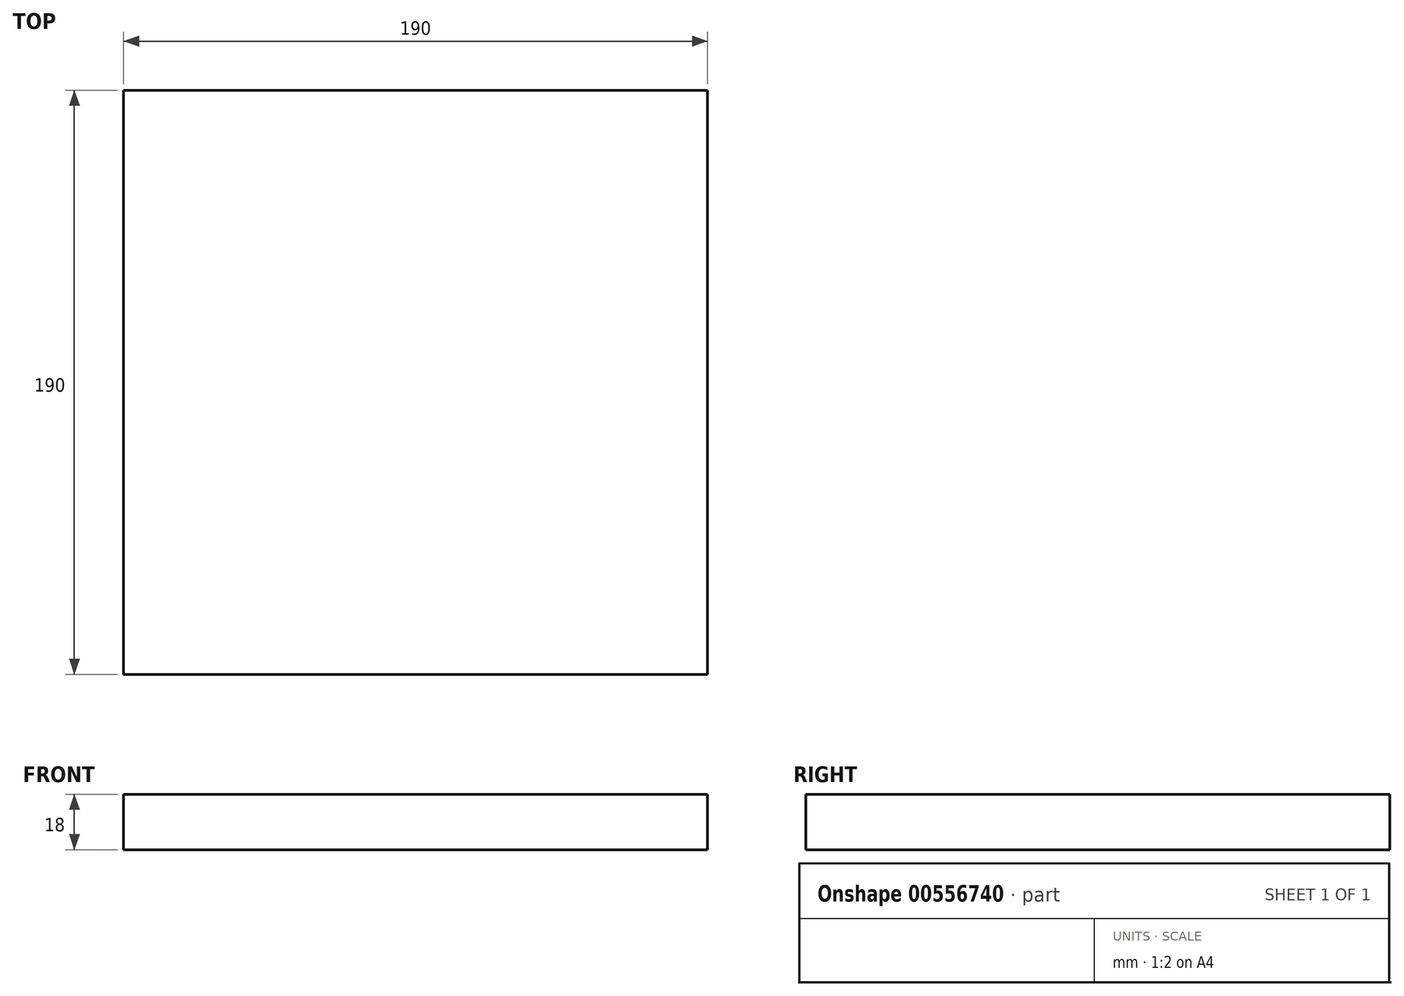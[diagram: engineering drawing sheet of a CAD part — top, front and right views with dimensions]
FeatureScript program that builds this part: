
annotation { "Feature Type Name" : "Feature", "Feature Type Description" : "" }
export const myFeature = defineFeature(function(context is Context, id is Id, definition is map)
    precondition{}
    {
        {
            var Q0;
            Q0=qCreatedBy(makeId("Top.planeOp"),FACE);
            var sketch = newSketch(context, id + "F0", { "sketchPlane" : qUnion([Q0])});
            skLineSegment(sketch, "E0", {"start": v(0, 0) * mm, "end": v(0, 190) * mm});
            skLineSegment(sketch, "E1", {"start": v(0, 190) * mm, "end": v(190, 190) * mm});
            skLineSegment(sketch, "E2", {"start": v(190, 190) * mm, "end": v(190, 0) * mm});
            skLineSegment(sketch, "E3", {"start": v(0, 0) * mm, "end": v(190, 0) * mm});
            skSolve(sketch);
        }
        {
            var Q0;
            Q0=makeQuery(id+"F0.imprint","IMPRINT",FACE,{"disambiguationData":[TD([[makeQuery(id+"F0.imprint","IMPRINT",EDGE,{"derivedFrom":sQuery(id+"F0.wireOp",EDGE,"E0")}),-1.0]])]});
            extrude(context, id + "F1", {"entities" : qUnion([Q0]), "endBound" : BoundingType.SYMMETRIC, "depth" : 12 * mm, "offsetDistance" : 25 * mm});
        }
        {
            var Q0;
            Q0=makeQuery(id+"F1.opExtrude","CAP_FACE",FACE,{"disambiguationData":[OSD([sQuery(id+"F0.wireOp",EDGE,"E0"),sQuery(id+"F0.wireOp",EDGE,"E1"),sQuery(id+"F0.wireOp",EDGE,"E2"),sQuery(id+"F0.wireOp",EDGE,"E3")])],"isStart":false});
            extrude(context, id + "F2", {"entities" : qUnion([Q0]), "operationType" : NewBodyOperationType.ADD, "endBound" : BoundingType.SYMMETRIC, "depth" : 12 * mm, "offsetDistance" : 25 * mm});
        }
    });
